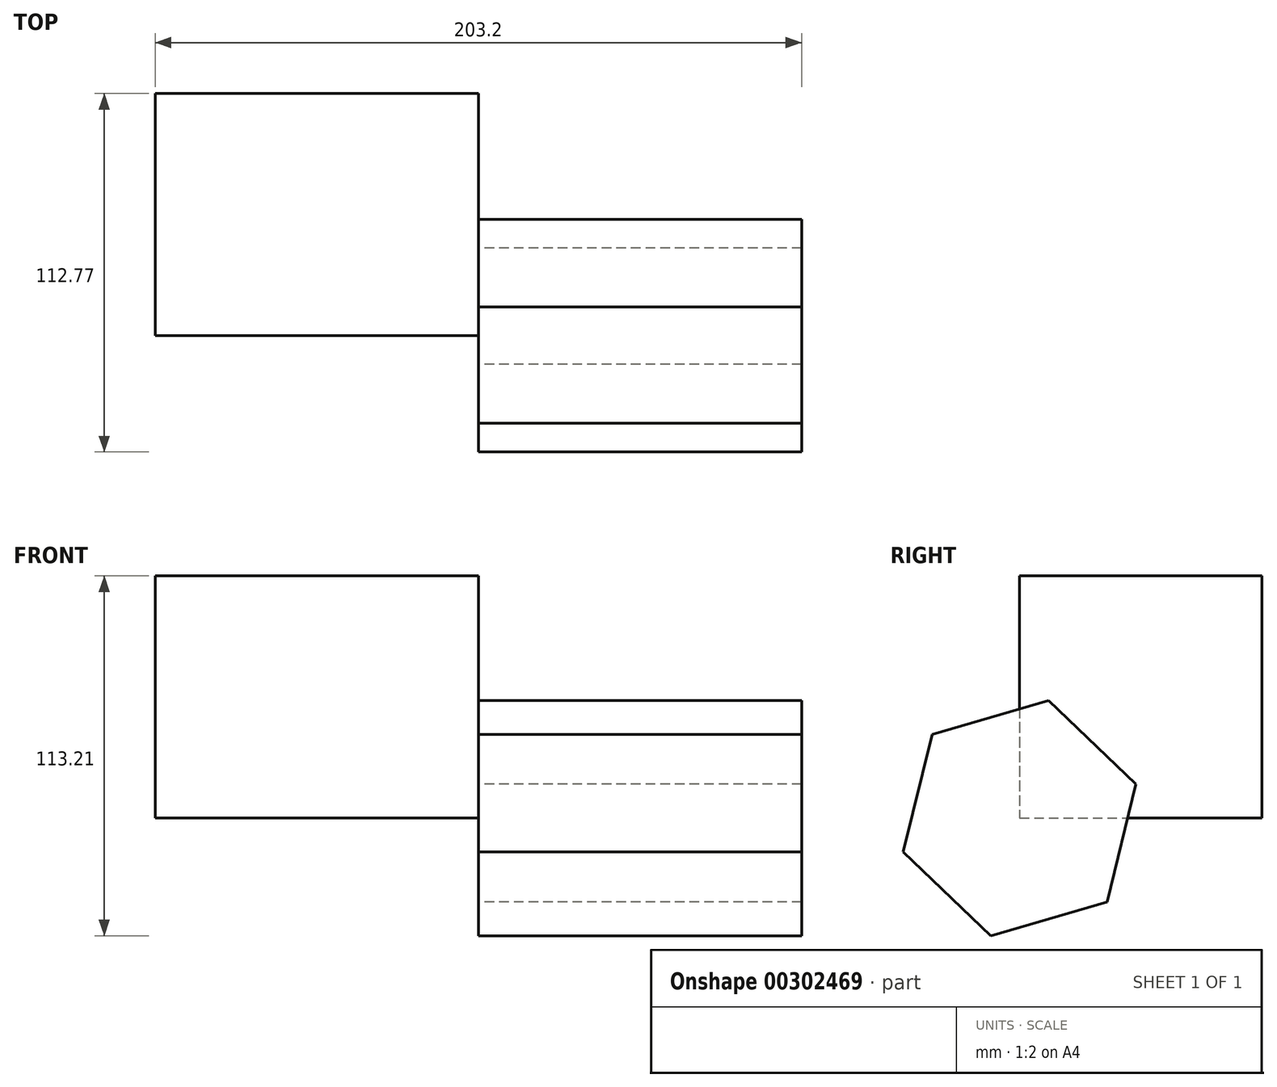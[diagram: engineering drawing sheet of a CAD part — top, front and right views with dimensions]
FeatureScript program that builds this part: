
annotation { "Feature Type Name" : "Feature", "Feature Type Description" : "" }
export const myFeature = defineFeature(function(context is Context, id is Id, definition is map)
    precondition{}
    {
        {
            var Q0;
            Q0=qCreatedBy(makeId("Right.planeOp"),FACE);
            var sketch = newSketch(context, id + "F0", { "sketchPlane" : qUnion([Q0])});
            skLineSegment(sketch, "E0", {"start": v(0, 0) * mm, "end": v(76.2, 0) * mm});
            skLineSegment(sketch, "E1", {"start": v(76.2, 0) * mm, "end": v(76.2, 76.2) * mm});
            skLineSegment(sketch, "E2", {"start": v(76.2, 76.2) * mm, "end": v(0, 76.2) * mm});
            skLineSegment(sketch, "E3", {"start": v(0, 76.2) * mm, "end": v(0, 0) * mm});
            skSolve(sketch);
        }
        {
            var Q0;
            Q0 = qSketchRegion(id + "F0", true);
            extrude(context, id + "F1", {"entities" : qUnion([Q0]), "depth" : 101.6 * mm});
        }
        {
            var Q0;
            Q0=makeQuery(id+"F1.opExtrude","CAP_FACE",FACE,{"disambiguationData":[OSD([sQuery(id+"F0.wireOp",EDGE,"E0"),sQuery(id+"F0.wireOp",EDGE,"E1"),sQuery(id+"F0.wireOp",EDGE,"E2"),sQuery(id+"F0.wireOp",EDGE,"E3")])],"isStart":false});
            var sketch = newSketch(context, id + "F2", { "sketchPlane" : qUnion([Q0])});
            skCircle(sketch, "E4.cCircle", {"center": v(0, 0) * mm, "radius": 33 * mm, "construction": true});
            skLineSegment(sketch, "E4.0", {"start": v(-36.57, -10.69) * mm, "end": v(-27.54, 26.33) * mm});
            skLineSegment(sketch, "E4.1", {"start": v(-27.54, 26.33) * mm, "end": v(9.03, 37.01) * mm});
            skLineSegment(sketch, "E4.2", {"start": v(9.03, 37.01) * mm, "end": v(36.57, 10.69) * mm});
            skLineSegment(sketch, "E4.3", {"start": v(36.57, 10.69) * mm, "end": v(27.54, -26.33) * mm});
            skLineSegment(sketch, "E4.4", {"start": v(27.54, -26.33) * mm, "end": v(-9.03, -37.01) * mm});
            skLineSegment(sketch, "E4.5", {"start": v(-9.03, -37.01) * mm, "end": v(-36.57, -10.69) * mm});
            skPoint(sketch, "E4.0.midPoint", {"position": v(-32.06, 7.82) * mm});
            skSolve(sketch);
        }
        {
            var Q0;
            {var subQ2=sQuery(id+"F2.wireOp",EDGE,"E4.0");Q0=makeQuery(id+"F2.imprint","IMPRINT",FACE,{"disambiguationData":[TD([[makeQuery(id+"F2.imprint","IMPRINT",EDGE,{"derivedFrom":subQ2}),-1.0]])]});}
            var Q1;
            {var subQ5=sQuery(id+"F2.wireOp",EDGE,"E4.2");Q1=makeQuery(id+"F2.imprint","IMPRINT",FACE,{"disambiguationData":[TD([[makeQuery(id+"F2.imprint","IMPRINT",EDGE,{"derivedFrom":subQ5}),-1.0]])]});}
            extrude(context, id + "F3", {"entities" : qUnion([Q0, Q1]), "operationType" : NewBodyOperationType.ADD, "depth" : 101.6 * mm});
        }
    });
